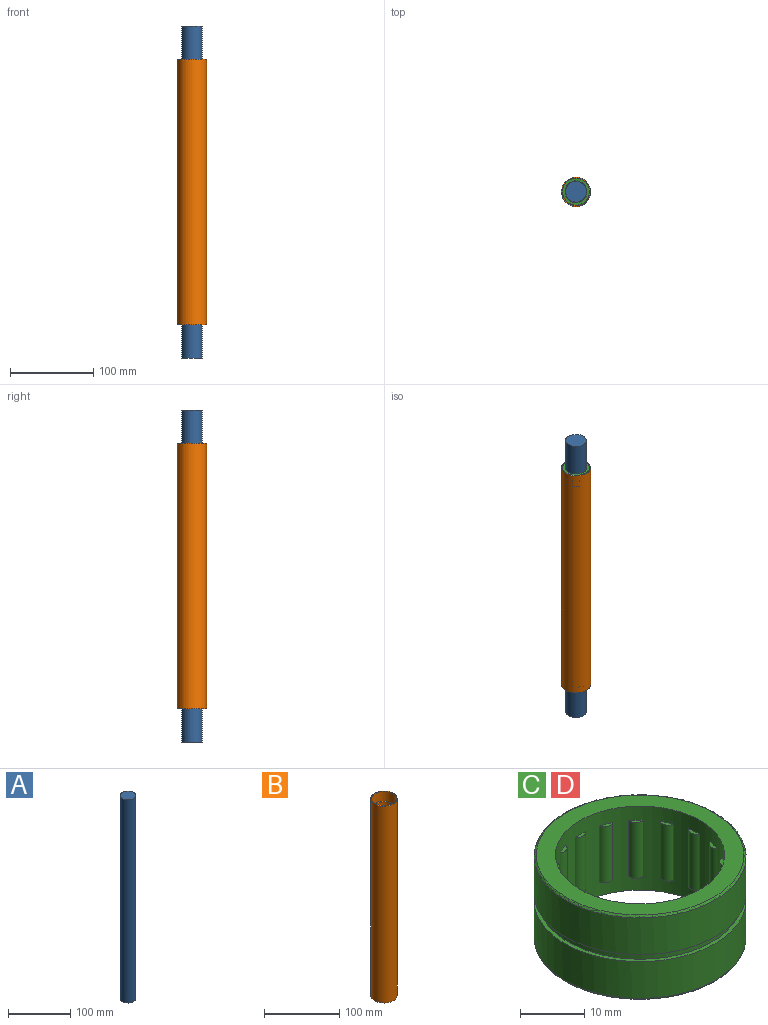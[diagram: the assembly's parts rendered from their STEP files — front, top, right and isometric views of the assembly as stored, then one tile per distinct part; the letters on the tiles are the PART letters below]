
ASSEMBLY  parts=4 mates=3
PART A: 3 faces, bbox 25x25x400 mm
  f0: cylinder r=12.5mm len=400mm, axis (0,0,-1), area 31415.9mm2, adj f1,f2
  f1: plane 25x25mm, normal (0,0,1), area 490.9mm2, adj f0
  f2: plane 25x25mm, normal (0,0,-1), area 490.9mm2, adj f0
PART B: 8 faces, bbox 35x35x320 mm
  f0: cylinder r=16.5mm len=33mm, axis (0,0,-1), area 1658.8mm2, adj f4,f7
  f1: cylinder r=16.5mm len=33mm, axis (0,0,-1), area 1658.8mm2, adj f3,f6
  f2: cylinder r=17.5mm len=320mm, axis (0,0,-1), area 35185.8mm2, adj f3,f4
  f3: plane 35x35mm, normal (0,0,1), area 106.8mm2, adj f1,f2
  f4: plane 35x35mm, normal (0,0,-1), area 106.8mm2, adj f0,f2
  f5: cylinder r=15mm len=288mm, axis (0,0,-1), area 27143.4mm2, adj f6,f7
  f6: plane 33x33mm, normal (0,0,1), area 148.4mm2, adj f1,f5
  f7: plane 33x33mm, normal (0,0,-1), area 148.4mm2, adj f0,f5
PART C: 63 faces, bbox 35.7x35.7x16 mm
  f0: cylinder r=0.42mm len=0.83mm, axis (-1,0,0), area 1.5mm2, adj f1,f11
  f1: cylinder r=15.83mm len=31.67mm, axis (0,0,1), area 131.8mm2, adj f0,f9,f10
  f2: cylinder r=16.5mm len=33mm, axis (0,0,1), area 726.2mm2, adj f8,f9
  f3: cylinder r=16.5mm len=33mm, axis (0,0,1), area 726.2mm2, adj f7,f10
  f4: plane 32.34x32.34mm, normal (0,0,1), area 276.1mm2, adj f5,f8
  f5: cylinder r=13.17mm len=26.35mm, axis (0,0,1), area 916.3mm2, adj f4,f6,f12,f13,f14,f15,f16,f17
  f6: plane 32.34x32.34mm, normal (0,0,-1), area 276.1mm2, adj f5,f7
  f7: torus R=16.17mm, axis (0,0,1), area 53.3mm2, adj f3,f6
  f8: torus R=16.17mm, axis (0,0,-1), area 53.3mm2, adj f2,f4
  f9: plane 33x33mm, normal (0,0,-1), area 67.6mm2, adj f1,f2
  f10: plane 33x33mm, normal (0,0,1), area 67.6mm2, adj f1,f3
  f11: cylinder r=15.27mm len=0.83mm, axis (0,0,-1), area 0.5mm2, adj f0
  f12: plane 2.09x1.07mm, normal (0,0,-1), area 1mm2, adj f5,f14
  f13: plane 2.09x1.07mm, normal (0,0,1), area 1mm2, adj f5,f14
  f14: cylinder r=1.33mm len=10.68mm, axis (0,0,1), area 28.6mm2, adj f5,f12,f13
  f15: plane 1.68x1.56mm, normal (0,0,-1), area 1mm2, adj f5,f17
  f16: plane 1.68x1.56mm, normal (0,0,1), area 1mm2, adj f5,f17
  f17: cylinder r=1.33mm len=10.68mm, axis (0,0,1), area 28.6mm2, adj f5,f15,f16
  f18: plane 1.91x1.32mm, normal (0,0,-1), area 1mm2, adj f5,f20
  f19: plane 1.91x1.32mm, normal (0,0,1), area 1mm2, adj f5,f20
  f20: cylinder r=1.33mm len=10.68mm, axis (0,0,1), area 28.6mm2, adj f5,f18,f19
  f21: plane 1.8x1.44mm, normal (0,0,-1), area 1mm2, adj f5,f23
  f22: plane 1.8x1.44mm, normal (0,0,1), area 1mm2, adj f5,f23
  f23: cylinder r=1.33mm len=10.68mm, axis (0,0,1), area 28.6mm2, adj f5,f21,f22
  f24: plane 2.24x0.72mm, normal (0,0,-1), area 1mm2, adj f5,f26
  f25: plane 2.24x0.72mm, normal (0,0,1), area 1mm2, adj f5,f26
  f26: cylinder r=1.33mm len=10.68mm, axis (0,0,1), area 28.6mm2, adj f5,f24,f25
  f27: plane 2.01x1.19mm, normal (0,0,-1), area 1mm2, adj f5,f29
  f28: plane 2.01x1.19mm, normal (0,0,1), area 1mm2, adj f5,f29
  f29: cylinder r=1.33mm len=10.68mm, axis (0,0,1), area 28.6mm2, adj f5,f27,f28
  f30: plane 2.21x0.84mm, normal (0,0,-1), area 1mm2, adj f5,f32
  f31: plane 2.21x0.84mm, normal (0,0,1), area 1mm2, adj f5,f32
  f32: cylinder r=1.33mm len=10.68mm, axis (0,0,1), area 28.6mm2, adj f5,f30,f31
  f33: plane 2.16x0.95mm, normal (0,0,-1), area 1mm2, adj f5,f35
  f34: plane 2.16x0.95mm, normal (0,0,1), area 1mm2, adj f5,f35
  f35: cylinder r=1.33mm len=10.68mm, axis (0,0,1), area 28.6mm2, adj f5,f33,f34
  f36: plane 2.21x0.84mm, normal (0,0,-1), area 1mm2, adj f5,f38
  f37: plane 2.21x0.84mm, normal (0,0,1), area 1mm2, adj f5,f38
  f38: cylinder r=1.33mm len=10.68mm, axis (0,0,1), area 28.6mm2, adj f5,f36,f37
  f39: plane 1.91x1.32mm, normal (0,0,-1), area 1mm2, adj f5,f41
  f40: plane 1.91x1.32mm, normal (0,0,1), area 1mm2, adj f5,f41
  f41: cylinder r=1.33mm len=10.68mm, axis (0,0,1), area 28.6mm2, adj f5,f39,f40
  f42: plane 1.8x1.44mm, normal (0,0,-1), area 1mm2, adj f5,f44
  f43: plane 1.8x1.44mm, normal (0,0,1), area 1mm2, adj f5,f44
  f44: cylinder r=1.33mm len=10.68mm, axis (0,0,1), area 28.6mm2, adj f5,f42,f43
  f45: plane 1.68x1.56mm, normal (0,0,-1), area 1mm2, adj f5,f47
  f46: plane 1.68x1.56mm, normal (0,0,1), area 1mm2, adj f5,f47
  f47: cylinder r=1.33mm len=10.68mm, axis (0,0,1), area 28.6mm2, adj f5,f45,f46
  f48: plane 2.01x1.19mm, normal (0,0,-1), area 1mm2, adj f5,f50
  f49: plane 2.01x1.19mm, normal (0,0,1), area 1mm2, adj f5,f50
  f50: cylinder r=1.33mm len=10.68mm, axis (0,0,1), area 28.6mm2, adj f5,f48,f49
  f51: plane 2.24x0.72mm, normal (0,0,-1), area 1mm2, adj f5,f53
  f52: plane 2.24x0.72mm, normal (0,0,1), area 1mm2, adj f5,f53
  f53: cylinder r=1.33mm len=10.68mm, axis (0,0,1), area 28.6mm2, adj f5,f51,f52
  f54: plane 2.16x0.95mm, normal (0,0,-1), area 1mm2, adj f5,f56
  f55: plane 2.16x0.95mm, normal (0,0,1), area 1mm2, adj f5,f56
  f56: cylinder r=1.33mm len=10.68mm, axis (0,0,1), area 28.6mm2, adj f5,f54,f55
  f57: plane 2.25x0.67mm, normal (0,0,-1), area 1mm2, adj f5,f59
  f58: plane 2.25x0.67mm, normal (0,0,1), area 1mm2, adj f5,f59
  f59: cylinder r=1.33mm len=10.68mm, axis (0,0,1), area 28.6mm2, adj f5,f57,f58
  f60: plane 2.09x1.07mm, normal (0,0,-1), area 1mm2, adj f5,f62
  f61: plane 2.09x1.07mm, normal (0,0,1), area 1mm2, adj f5,f62
  f62: cylinder r=1.33mm len=10.68mm, axis (0,0,1), area 28.6mm2, adj f5,f60,f61
PART D: same geometry as C
PLACE A t=(-0.02,0.03,152.06)mm
PLACE B rot(axis=(1,0,0),180deg) t=(6.91,2.34,152.06)mm
PLACE C rot(axis=(1,0,0),180deg) t=(-0.02,0.03,304.06)mm
PLACE D t=(-0.02,0.03,0.06)mm
MATE revolute A.f0 <-> B.f0  axis (0,0,-1) through (-0.02,0.03,152.06)mm
MATE fastened B.f0 <-> C.f8  axis (0,0,1) through (-0.02,0.03,296.06)mm
MATE fastened B.f0 <-> D.f8  axis (0,0,-1) through (-0.02,0.03,8.06)mm
